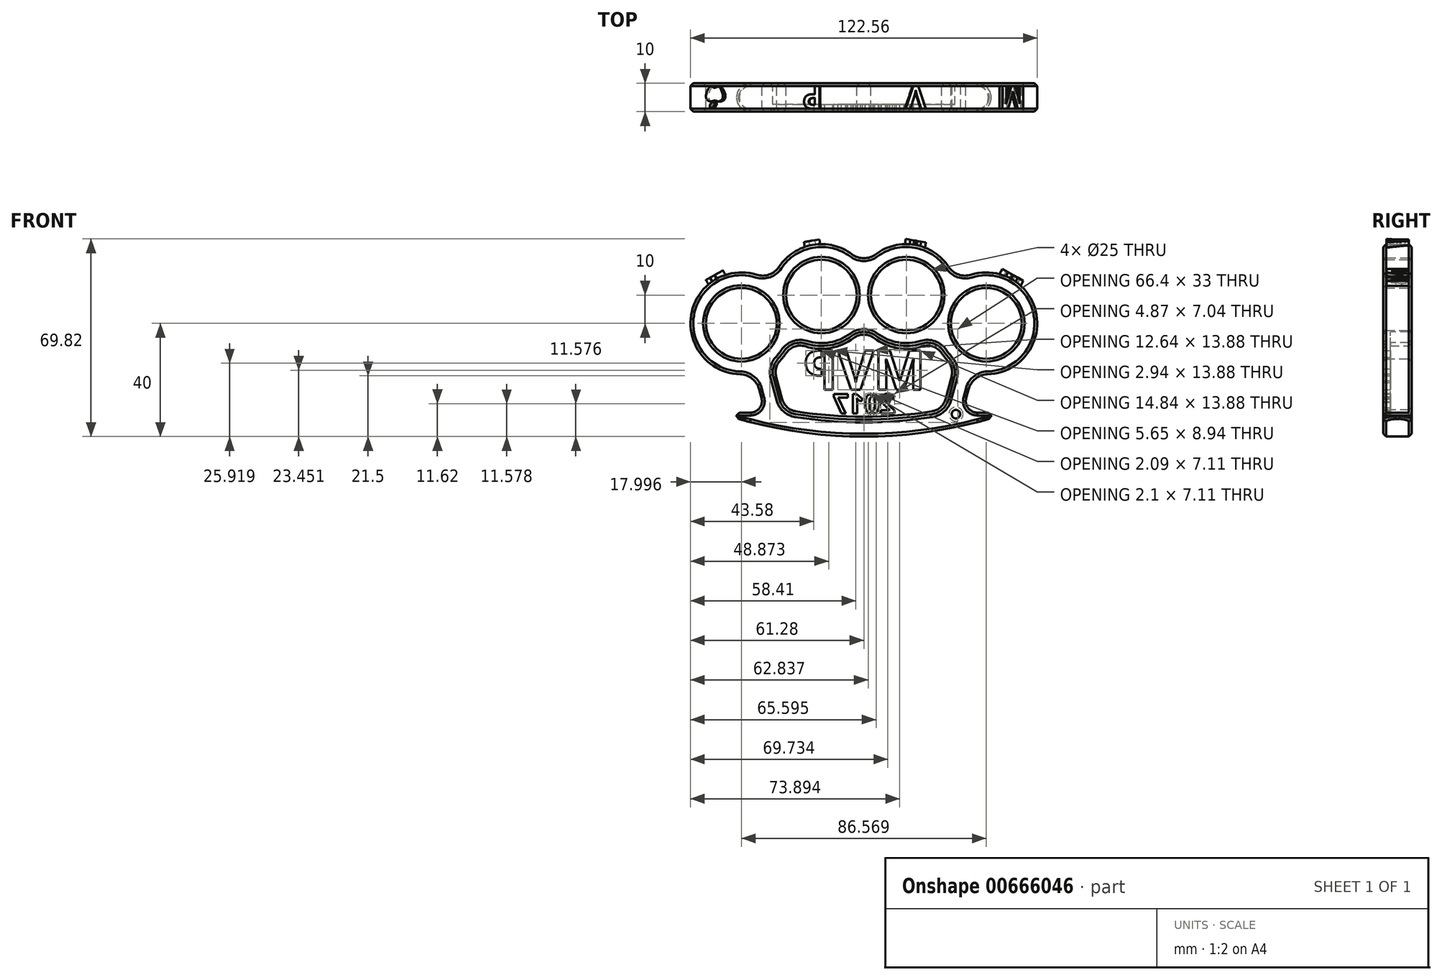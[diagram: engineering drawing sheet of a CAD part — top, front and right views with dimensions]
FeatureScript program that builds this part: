
annotation { "Feature Type Name" : "Feature", "Feature Type Description" : "" }
export const myFeature = defineFeature(function(context is Context, id is Id, definition is map)
    precondition{}
    {
        {
            var Q0;
            Q0=qCreatedBy(makeId("Front.planeOp"),FACE);
            var sketch = newSketch(context, id + "F0", { "sketchPlane" : qUnion([Q0])});
            skCircle(sketch, "E0", {"center": v(-43.28, 0) * mm, "radius": 12.5 * mm});
            skCircle(sketch, "E1", {"center": v(-15, 10) * mm, "radius": 12.5 * mm});
            skCircle(sketch, "E2", {"center": v(15, 10) * mm, "radius": 12.5 * mm});
            skCircle(sketch, "E3", {"center": v(43.28, 0) * mm, "radius": 12.5 * mm});
            skLineSegment(sketch, "E4", {"start": v(0, 38.87) * mm, "end": v(0, -56.1) * mm, "construction": true});
            skArc(sketch, "E5", {"start": v(-32.46, 14.38) * mm, "mid": v(-60.95, 3.43) * mm, "end": v(-38.63, -17.39) * mm});
            skArc(sketch, "E6", {"start": v(25.83, -4.38) * mm, "mid": v(28.5, -10.27) * mm, "end": v(33.1, -14.84) * mm});
            skArc(sketch, "E7.trimOffspring", {"start": v(-25.83, -4.38) * mm, "mid": v(-11.96, -7.74) * mm, "end": v(0, 0.05) * mm});
            skArc(sketch, "E8.trimOffspring", {"start": v(32.46, 14.38) * mm, "mid": v(18.04, 27.74) * mm, "end": v(0, 19.95) * mm});
            skArc(sketch, "E9.trimOffspring", {"start": v(0, 19.95) * mm, "mid": v(-18.04, 27.74) * mm, "end": v(-32.46, 14.38) * mm});
            skArc(sketch, "E10.trimOffspring", {"start": v(0, 0.05) * mm, "mid": v(11.96, -7.74) * mm, "end": v(25.83, -4.38) * mm});
            skArc(sketch, "E11", {"start": v(-45, -33.54) * mm, "mid": v(0, -40) * mm, "end": v(45, -33.54) * mm});
            skLineSegment(sketch, "E12", {"start": v(-45, -33.54) * mm, "end": v(-45, -31.54) * mm});
            skLineSegment(sketch, "E13", {"start": v(-36.18, -26.5) * mm, "end": v(-38.63, -17.39) * mm});
            skLineSegment(sketch, "E14", {"start": v(-45, -31.54) * mm, "end": v(-40.05, -31.54) * mm});
            skLineSegment(sketch, "E15.MirrorCS", {"start": v(45, -33.54) * mm, "end": v(45, -31.54) * mm});
            skPoint(sketch, "E16.visualSharp", {"position": v(-34.83, -31.54) * mm});
            skArc(sketch, "E16.filletArc", {"start": v(-40.05, -31.54) * mm, "mid": v(-36.87, -29.98) * mm, "end": v(-36.18, -26.5) * mm});
            skLineSegment(sketch, "E17.MirrorCS", {"start": v(36.18, -26.5) * mm, "end": v(38.63, -17.39) * mm});
            skLineSegment(sketch, "E18.MirrorCS", {"start": v(45, -31.54) * mm, "end": v(40.05, -31.54) * mm});
            skArc(sketch, "E19.MirrorCS", {"start": v(40.05, -31.54) * mm, "mid": v(36.87, -29.98) * mm, "end": v(36.18, -26.5) * mm});
            skArc(sketch, "E20", {"start": v(-28.68, -31.3) * mm, "mid": v(0, -34) * mm, "end": v(28.68, -31.3) * mm});
            skLineSegment(sketch, "E21", {"start": v(-28.68, -31.3) * mm, "end": v(-33.1, -14.84) * mm});
            skLineSegment(sketch, "E22", {"start": v(28.68, -31.3) * mm, "end": v(33.1, -14.84) * mm});
            skArc(sketch, "E23.trimOffspring", {"start": v(-33.1, -14.84) * mm, "mid": v(-28.5, -10.27) * mm, "end": v(-25.83, -4.38) * mm});
            skArc(sketch, "E24.trimOffspring", {"start": v(38.63, -17.39) * mm, "mid": v(60.95, 3.43) * mm, "end": v(32.46, 14.38) * mm});
            skSolve(sketch);
        }
        {
            var Q0;
            Q0=makeQuery(id+"F0.imprint","IMPRINT",FACE,{"disambiguationData":[TD([[makeQuery(id+"F0.imprint","IMPRINT",EDGE,{"derivedFrom":sQuery(id+"F0.wireOp",EDGE,"E0")}),-1.0]])]});
            extrude(context, id + "F1", {"entities" : qUnion([Q0]), "depth" : 10 * mm, "offsetDistance" : 25 * mm});
        }
        {
            var Q0;
            Q0=makeQuery(id+"F1.opExtrude","CAP_EDGE",EDGE,{"disambiguationData":[OSD([sQuery(id+"F0.wireOp",EDGE,"E12")])],"isStart":false});
            var Q1;
            Q1=makeQuery(id+"F1.opExtrude","CAP_EDGE",EDGE,{"disambiguationData":[OSD([sQuery(id+"F0.wireOp",EDGE,"E12")])],"isStart":true});
            var Q2;
            Q2=makeQuery(id+"F1.opExtrude","CAP_EDGE",EDGE,{"disambiguationData":[OSD([sQuery(id+"F0.wireOp",EDGE,"E15.MirrorCS")])],"isStart":false});
            var Q3;
            Q3=makeQuery(id+"F1.opExtrude","CAP_EDGE",EDGE,{"disambiguationData":[OSD([sQuery(id+"F0.wireOp",EDGE,"E15.MirrorCS")])],"isStart":true});
            fillet(context, id + "F2", {"entities" : qUnion([Q0, Q1, Q2, Q3]), "radius" : 5 * mm, "tangentPropagation" : true, "allowEdgeOverflow" : false});
        }
        {
            var Q0;
            Q0=makeQuery(id+"F1.opExtrude","SWEPT_EDGE",EDGE,{"disambiguationData":[OSD([sQuery(id+"F0.wireOp",EDGE,"E7.trimOffspring"),sQuery(id+"F0.wireOp",EDGE,"E23.trimOffspring")])]});
            var Q1;
            Q1=makeQuery(id+"F1.opExtrude","SWEPT_EDGE",EDGE,{"disambiguationData":[OSD([sQuery(id+"F0.wireOp",EDGE,"E7.trimOffspring"),sQuery(id+"F0.wireOp",EDGE,"E10.trimOffspring")])]});
            var Q2;
            Q2=makeQuery(id+"F1.opExtrude","SWEPT_EDGE",EDGE,{"disambiguationData":[OSD([sQuery(id+"F0.wireOp",EDGE,"E6"),sQuery(id+"F0.wireOp",EDGE,"E10.trimOffspring")])]});
            var Q3;
            Q3=makeQuery(id+"F1.opExtrude","SWEPT_EDGE",EDGE,{"disambiguationData":[OSD([sQuery(id+"F0.wireOp",EDGE,"E6"),sQuery(id+"F0.wireOp",EDGE,"E22")])]});
            var Q4;
            Q4=makeQuery(id+"F1.opExtrude","SWEPT_EDGE",EDGE,{"disambiguationData":[OSD([sQuery(id+"F0.wireOp",EDGE,"E21"),sQuery(id+"F0.wireOp",EDGE,"E23.trimOffspring")])]});
            var Q5;
            Q5=makeQuery(id+"F1.opExtrude","SWEPT_EDGE",EDGE,{"disambiguationData":[OSD([sQuery(id+"F0.wireOp",EDGE,"E8.trimOffspring"),sQuery(id+"F0.wireOp",EDGE,"E24.trimOffspring")])]});
            var Q6;
            Q6=makeQuery(id+"F1.opExtrude","SWEPT_EDGE",EDGE,{"disambiguationData":[OSD([sQuery(id+"F0.wireOp",EDGE,"E8.trimOffspring"),sQuery(id+"F0.wireOp",EDGE,"E9.trimOffspring")])]});
            var Q7;
            Q7=makeQuery(id+"F1.opExtrude","SWEPT_EDGE",EDGE,{"disambiguationData":[OSD([sQuery(id+"F0.wireOp",EDGE,"E5"),sQuery(id+"F0.wireOp",EDGE,"E9.trimOffspring")])]});
            var Q8;
            Q8=makeQuery(id+"F1.opExtrude","SWEPT_EDGE",EDGE,{"disambiguationData":[OSD([sQuery(id+"F0.wireOp",EDGE,"E20"),sQuery(id+"F0.wireOp",EDGE,"E21")])]});
            var Q9;
            Q9=makeQuery(id+"F1.opExtrude","SWEPT_EDGE",EDGE,{"disambiguationData":[OSD([sQuery(id+"F0.wireOp",EDGE,"E20"),sQuery(id+"F0.wireOp",EDGE,"E22")])]});
            var Q10;
            Q10=makeQuery(id+"F1.opExtrude","SWEPT_EDGE",EDGE,{"disambiguationData":[OSD([sQuery(id+"F0.wireOp",EDGE,"E5"),sQuery(id+"F0.wireOp",EDGE,"E13")])]});
            var Q11;
            Q11=makeQuery(id+"F1.opExtrude","SWEPT_EDGE",EDGE,{"disambiguationData":[OSD([sQuery(id+"F0.wireOp",EDGE,"E17.MirrorCS"),sQuery(id+"F0.wireOp",EDGE,"E24.trimOffspring")])]});
            fillet(context, id + "F3", {"entities" : qUnion([Q0, Q1, Q2, Q3, Q4, Q5, Q6, Q7, Q8, Q9, Q10, Q11]), "radius" : 7 * mm, "tangentPropagation" : true, "allowEdgeOverflow" : false});
        }
        {
            var Q0;
            Q0=qCreatedBy(makeId("Front.planeOp"),FACE);
            cPlane(context, id + "F4", {"entities" : qUnion([Q0]), "cplaneType" : CPlaneType.OFFSET, "offset" : 5 * mm, "width" : 150 * mm, "height" : 150 * mm});
        }
        {
            var Q0;
            Q0=makeQuery(id+"F1.opExtrude","CAP_FACE",FACE,{"disambiguationData":[OSD([sQuery(id+"F0.wireOp",EDGE,"E0"),sQuery(id+"F0.wireOp",EDGE,"E1"),sQuery(id+"F0.wireOp",EDGE,"E2"),sQuery(id+"F0.wireOp",EDGE,"E3"),sQuery(id+"F0.wireOp",EDGE,"E5"),sQuery(id+"F0.wireOp",EDGE,"E6"),sQuery(id+"F0.wireOp",EDGE,"E7.trimOffspring"),sQuery(id+"F0.wireOp",EDGE,"E8.trimOffspring"),sQuery(id+"F0.wireOp",EDGE,"E9.trimOffspring"),sQuery(id+"F0.wireOp",EDGE,"E10.trimOffspring"),sQuery(id+"F0.wireOp",EDGE,"E11"),sQuery(id+"F0.wireOp",EDGE,"E12"),sQuery(id+"F0.wireOp",EDGE,"E13"),sQuery(id+"F0.wireOp",EDGE,"E14"),sQuery(id+"F0.wireOp",EDGE,"E15.MirrorCS"),sQuery(id+"F0.wireOp",EDGE,"E16.filletArc"),sQuery(id+"F0.wireOp",EDGE,"E17.MirrorCS"),sQuery(id+"F0.wireOp",EDGE,"E18.MirrorCS"),sQuery(id+"F0.wireOp",EDGE,"E19.MirrorCS"),sQuery(id+"F0.wireOp",EDGE,"E20"),sQuery(id+"F0.wireOp",EDGE,"E21"),sQuery(id+"F0.wireOp",EDGE,"E22"),sQuery(id+"F0.wireOp",EDGE,"E23.trimOffspring"),sQuery(id+"F0.wireOp",EDGE,"E24.trimOffspring")])],"isStart":false});
            var sketch = newSketch(context, id + "F5", { "sketchPlane" : qUnion([Q0])});
            skLineSegment(sketch, "E25.0", {"start": v(-29.84, -26.99) * mm, "end": v(-31.96, -19.07) * mm});
            skArc(sketch, "E25.1", {"start": v(-24.18, -32.1) * mm, "mid": v(-27.76, -30.38) * mm, "end": v(-29.84, -26.99) * mm});
            skArc(sketch, "E25.2", {"start": v(-24.18, -32.1) * mm, "mid": v(0, -34) * mm, "end": v(24.18, -32.1) * mm});
            skArc(sketch, "E25.3", {"start": v(29.84, -26.99) * mm, "mid": v(27.76, -30.38) * mm, "end": v(24.18, -32.1) * mm});
            skLineSegment(sketch, "E25.4", {"start": v(29.84, -26.99) * mm, "end": v(31.96, -19.07) * mm});
            skArc(sketch, "E25.5", {"start": v(30.26, -12.43) * mm, "mid": v(31.98, -15.53) * mm, "end": v(31.96, -19.07) * mm});
            skArc(sketch, "E25.6", {"start": v(20.38, -7.18) * mm, "mid": v(24.8, -7.26) * mm, "end": v(28.3, -9.98) * mm});
            skArc(sketch, "E25.7", {"start": v(4.2, -4.4) * mm, "mid": v(11.96, -7.74) * mm, "end": v(20.38, -7.18) * mm});
            skArc(sketch, "E25.8", {"start": v(-4.2, -4.4) * mm, "mid": v(0, -3) * mm, "end": v(4.2, -4.4) * mm});
            skArc(sketch, "E25.9", {"start": v(-20.38, -7.18) * mm, "mid": v(-11.96, -7.74) * mm, "end": v(-4.2, -4.4) * mm});
            skArc(sketch, "E25.10", {"start": v(-28.3, -9.98) * mm, "mid": v(-24.8, -7.26) * mm, "end": v(-20.38, -7.18) * mm});
            skArc(sketch, "E25.11", {"start": v(-31.96, -19.07) * mm, "mid": v(-31.98, -15.53) * mm, "end": v(-30.26, -12.43) * mm});
            skArc(sketch, "E25.12", {"start": v(-30.26, -12.43) * mm, "mid": v(-29.23, -11.25) * mm, "end": v(-28.3, -9.98) * mm});
            skArc(sketch, "E25.13", {"start": v(28.3, -9.98) * mm, "mid": v(29.23, -11.25) * mm, "end": v(30.26, -12.43) * mm});
            skSolve(sketch);
        }
        {
            var Q0;
            Q0 = qSketchRegion(id + "F5", true);
            extrude(context, id + "F6", {"entities" : qUnion([Q0]), "operationType" : NewBodyOperationType.ADD, "oppositeDirection" : true, "depth" : 2.5 * mm, "offsetDistance" : 25 * mm});
        }
        {
            var Q0;
            Q0=makeQuery(id+"F6.opExtrude","CAP_FACE",FACE,{"disambiguationData":[OSD([sQuery(id+"F5.wireOp",EDGE,"E25.0"),sQuery(id+"F5.wireOp",EDGE,"E25.1"),sQuery(id+"F5.wireOp",EDGE,"E25.2"),sQuery(id+"F5.wireOp",EDGE,"E25.3"),sQuery(id+"F5.wireOp",EDGE,"E25.4"),sQuery(id+"F5.wireOp",EDGE,"E25.5"),sQuery(id+"F5.wireOp",EDGE,"E25.6"),sQuery(id+"F5.wireOp",EDGE,"E25.7"),sQuery(id+"F5.wireOp",EDGE,"E25.8"),sQuery(id+"F5.wireOp",EDGE,"E25.9"),sQuery(id+"F5.wireOp",EDGE,"E25.10"),sQuery(id+"F5.wireOp",EDGE,"E25.11"),sQuery(id+"F5.wireOp",EDGE,"E25.12"),sQuery(id+"F5.wireOp",EDGE,"E25.13")])],"isStart":false});
            var sketch = newSketch(context, id + "F7", { "sketchPlane" : qUnion([Q0])});
            skText(sketch, "E26", { "text": "MVP", "fontName": "OpenSans-Bold.ttf"});
            skText(sketch, "E27", { "text": "2017", "fontName": "OpenSans-Bold.ttf"});
            const initialGuessF7  = {"E26": [-0.02178, -0.02349, 1, 0, 0.014], "E27": [-0.01126, -0.0319, 1, 0, 0.007]};
            skSetInitialGuess(sketch, initialGuessF7);
            skSolve(sketch);
        }
        {
            var Q0;
            Q0 = qSketchRegion(id + "F7", true);
            extrude(context, id + "F8", {"entities" : qUnion([Q0]), "operationType" : NewBodyOperationType.REMOVE, "oppositeDirection" : true, "depth" : 25 * mm, "offsetDistance" : 25 * mm});
        }
        {
            var Q0;
            Q0=makeQuery(id+"F1.opExtrude","CAP_EDGE",EDGE,{"disambiguationData":[OSD([sQuery(id+"F0.wireOp",EDGE,"E5")])],"isStart":false});
            var Q1;
            Q1=makeQuery(id+"F1.opExtrude","CAP_EDGE",EDGE,{"disambiguationData":[OSD([sQuery(id+"F0.wireOp",EDGE,"E11")])],"isStart":false});
            var Q2;
            Q2=makeQuery(id+"F1.opExtrude","CAP_EDGE",EDGE,{"disambiguationData":[OSD([sQuery(id+"F0.wireOp",EDGE,"E21")])],"isStart":false});
            var Q3;
            Q3=makeQuery(id+"F1.opExtrude","CAP_EDGE",EDGE,{"disambiguationData":[OSD([sQuery(id+"F0.wireOp",EDGE,"E0")])],"isStart":false});
            var Q4;
            Q4=makeQuery(id+"F1.opExtrude","CAP_EDGE",EDGE,{"disambiguationData":[OSD([sQuery(id+"F0.wireOp",EDGE,"E1")])],"isStart":false});
            var Q5;
            Q5=makeQuery(id+"F1.opExtrude","CAP_EDGE",EDGE,{"disambiguationData":[OSD([sQuery(id+"F0.wireOp",EDGE,"E2")])],"isStart":false});
            var Q6;
            Q6=makeQuery(id+"F1.opExtrude","CAP_EDGE",EDGE,{"disambiguationData":[OSD([sQuery(id+"F0.wireOp",EDGE,"E3")])],"isStart":false});
            var Q7;
            Q7=makeQuery(id+"F1.opExtrude","CAP_EDGE",EDGE,{"disambiguationData":[OSD([sQuery(id+"F0.wireOp",EDGE,"E3")])],"isStart":true});
            var Q8;
            Q8=makeQuery(id+"F1.opExtrude","CAP_EDGE",EDGE,{"disambiguationData":[OSD([sQuery(id+"F0.wireOp",EDGE,"E2")])],"isStart":true});
            var Q9;
            Q9=makeQuery(id+"F1.opExtrude","CAP_EDGE",EDGE,{"disambiguationData":[OSD([sQuery(id+"F0.wireOp",EDGE,"E1")])],"isStart":true});
            var Q10;
            Q10=makeQuery(id+"F1.opExtrude","CAP_EDGE",EDGE,{"disambiguationData":[OSD([sQuery(id+"F0.wireOp",EDGE,"E0")])],"isStart":true});
            var Q11;
            Q11=makeQuery(id+"F1.opExtrude","CAP_EDGE",EDGE,{"disambiguationData":[OSD([sQuery(id+"F0.wireOp",EDGE,"E22")])],"isStart":true});
            var Q12;
            Q12=makeQuery(id+"F6.opExtrude","CAP_EDGE",EDGE,{"disambiguationData":[OSD([sQuery(id+"F5.wireOp",EDGE,"E25.4")])],"isStart":true});
            var Q13;
            Q13=makeQuery(id+"F6.opExtrude","CAP_EDGE",EDGE,{"disambiguationData":[OSD([sQuery(id+"F5.wireOp",EDGE,"E25.5")])],"isStart":false});
            chamfer(context, id + "F9", {"entities" : qUnion([Q0, Q1, Q2, Q3, Q4, Q5, Q6, Q7, Q8, Q9, Q10, Q11, Q12, Q13]), "width" : 1 * mm, "tangentPropagation" : true});
        }
        {
            var Q0;
            Q0=qCreatedBy(id+"F4.planeOp",FACE);
            var sketch = newSketch(context, id + "F10", { "sketchPlane" : qUnion([Q0])});
            skLineSegment(sketch, "E28", {"start": v(0, -77.43) * mm, "end": v(19.89, 38.49) * mm, "construction": true});
            skLineSegment(sketch, "E29", {"start": v(0, 38.45) * mm, "end": v(0, -77.43) * mm, "construction": true});
            skLineSegment(sketch, "E30", {"start": v(0, -77.43) * mm, "end": v(-64.72, 38.35) * mm, "construction": true});
            skLineSegment(sketch, "E31", {"start": v(0, -77.43) * mm, "end": v(63.92, 36.9) * mm, "construction": true});
            skCircle(sketch, "E32.0", {"center": v(-43.28, 0) * mm, "radius": 12.5 * mm});
            skCircle(sketch, "E33.0", {"center": v(43.28, 0) * mm, "radius": 12.5 * mm});
            skPoint(sketch, "E34", {"position": v(-52.07, 15.71) * mm});
            skPoint(sketch, "E35", {"position": v(-18.04, 27.74) * mm});
            skPoint(sketch, "E36", {"position": v(18.04, 27.74) * mm});
            skPoint(sketch, "E37", {"position": v(52.07, 15.71) * mm});
            skLineSegment(sketch, "E38", {"start": v(0, -77.43) * mm, "end": v(-21.26, 46.47) * mm, "construction": true});
            skCircle(sketch, "E39.0", {"center": v(-15, 10) * mm, "radius": 12.5 * mm});
            skSolve(sketch);
        }
        {
            var Q0;
            Q0=sQuery(id+"F10.wireOp",VERTEX,"E34");
            var Q1;
            Q1=sQuery(id+"F10.wireOp",EDGE,"E30");
            cPlane(context, id + "F11", {"entities" : qUnion([Q0, Q1]), "cplaneType" : CPlaneType.LINE_POINT, "offset" : 25 * mm, "width" : 150 * mm, "height" : 150 * mm});
        }
        {
            var Q0;
            Q0=sQuery(id+"F10.wireOp",EDGE,"E38");
            var Q1;
            Q1=sQuery(id+"F10.wireOp",VERTEX,"E35");
            cPlane(context, id + "F12", {"entities" : qUnion([Q0, Q1]), "cplaneType" : CPlaneType.LINE_POINT, "offset" : 25 * mm, "width" : 150 * mm, "height" : 150 * mm});
        }
        {
            var Q0;
            Q0=sQuery(id+"F10.wireOp",VERTEX,"E36");
            var Q1;
            Q1=sQuery(id+"F10.wireOp",EDGE,"E28");
            cPlane(context, id + "F13", {"entities" : qUnion([Q0, Q1]), "cplaneType" : CPlaneType.LINE_POINT, "offset" : 25 * mm, "width" : 150 * mm, "height" : 150 * mm});
        }
        {
            var Q0;
            Q0=sQuery(id+"F10.wireOp",VERTEX,"E37");
            var Q1;
            Q1=sQuery(id+"F10.wireOp",EDGE,"E31");
            cPlane(context, id + "F14", {"entities" : qUnion([Q0, Q1]), "cplaneType" : CPlaneType.LINE_POINT, "offset" : 25 * mm, "width" : 150 * mm, "height" : 150 * mm});
        }
        {
            var Q0;
            Q0=qCreatedBy(id+"F14.planeOp",FACE);
            var sketch = newSketch(context, id + "F15", { "sketchPlane" : qUnion([Q0])});
            skText(sketch, "E40", { "text": "M", "fontName": "OpenSans-Bold.ttf"});
            skLineSegment(sketch, "E41", {"start": v(42.88, -1) * mm, "end": v(73.13, -1) * mm});
            const initialGuessF15  = {"E40": [0.04288, -0.001, -1, 0, 0.008]};
            skSetInitialGuess(sketch, initialGuessF15);
            skSolve(sketch);
        }
        {
            var Q0;
            Q0=qCreatedBy(id+"F13.planeOp",FACE);
            var sketch = newSketch(context, id + "F16", { "sketchPlane" : qUnion([Q0])});
            skText(sketch, "E42", { "text": "V", "fontName": "OpenSans-Bold.ttf"});
            skLineSegment(sketch, "E43", {"start": v(13.53, -1) * mm, "end": v(16.76, -1) * mm});
            const initialGuessF16  = {"E42": [0.01676, -0.001, -1, 0, 0.008]};
            skSetInitialGuess(sketch, initialGuessF16);
            skSolve(sketch);
        }
        {
            var Q0;
            Q0=qCreatedBy(id+"F12.planeOp",FACE);
            var sketch = newSketch(context, id + "F17", { "sketchPlane" : qUnion([Q0])});
            skText(sketch, "E44", { "text": "P", "fontName": "OpenSans-Bold.ttf"});
            skLineSegment(sketch, "E45", {"start": v(-9.5, -1) * mm, "end": v(27.08, -1) * mm});
            const initialGuessF17  = {"E44": [-0.0095, -0.001, -1, 0, 0.008]};
            skSetInitialGuess(sketch, initialGuessF17);
            skSolve(sketch);
        }
        {
            var Q0;
            Q0=qCreatedBy(id+"F11.planeOp",FACE);
            var sketch = newSketch(context, id + "F18", { "sketchPlane" : qUnion([Q0])});
            skLineSegment(sketch, "E46", {"start": v(-37.78, 4.33) * mm, "end": v(-37.78, -21.33) * mm, "construction": true});
            skFitSpline(sketch, "E47", {"points": [v(-37.78, -1.74) * mm, v(-39.38, -1.13) * mm, v(-40.33, -2.03) * mm, v(-41.18, -4.15) * mm, v(-40.94, -5.57) * mm, v(-39.59, -6.37) * mm, v(-37.78, -6) * mm], "startDerivative": vector(-11.84, 8.82) * mm, "endDerivative": vector(10.4, 4.73) * mm});
            skPoint(sketch, "E48", {"position": v(-37.78, -8.5) * mm});
            skFitSpline(sketch, "E49.MirrorCS", {"points": [v(-37.78, -1.74) * mm, v(-36.18, -1.13) * mm, v(-35.23, -2.03) * mm, v(-34.38, -4.15) * mm, v(-34.63, -5.57) * mm, v(-35.97, -6.37) * mm, v(-37.78, -6) * mm], "startDerivative": vector(11.84, 8.82) * mm, "endDerivative": vector(-10.4, 4.73) * mm});
            skArc(sketch, "E50.filletArc", {"start": v(-38.29, -1.4) * mm, "mid": v(-37.78, -1.54) * mm, "end": v(-37.27, -1.4) * mm});
            skArc(sketch, "E51.filletArc", {"start": v(-37.43, -6.16) * mm, "mid": v(-37.78, -6.1) * mm, "end": v(-38.13, -6.16) * mm});
            skArc(sketch, "E52", {"start": v(-37.78, -6.5) * mm, "mid": v(-39.26, -7.12) * mm, "end": v(-39.57, -8.7) * mm});
            skArc(sketch, "E53", {"start": v(-39.57, -8.7) * mm, "mid": v(-38.07, -8.1) * mm, "end": v(-37.78, -6.5) * mm});
            skSolve(sketch);
        }
        {
            var Q0;
            Q0 = qSketchRegion(id + "F18", true);
            extrude(context, id + "F19", {"entities" : qUnion([Q0]), "operationType" : NewBodyOperationType.ADD, "depth" : 1.5 * mm, "offsetDistance" : 25 * mm, "hasSecondDirection" : true, "secondDirectionBound" : SecondDirectionBoundingType.UP_TO_NEXT, "secondDirectionOppositeDirection" : true, "secondDirectionDepth" : 25 * mm});
        }
        {
            var Q0;
            Q0 = qSketchRegion(id + "F17", true);
            extrude(context, id + "F20", {"entities" : qUnion([Q0]), "operationType" : NewBodyOperationType.ADD, "depth" : 1.5 * mm, "offsetDistance" : 25 * mm, "hasSecondDirection" : true, "secondDirectionBound" : SecondDirectionBoundingType.UP_TO_NEXT, "secondDirectionOppositeDirection" : true, "secondDirectionDepth" : 25 * mm});
        }
        {
            var Q0;
            Q0 = qSketchRegion(id + "F16", true);
            extrude(context, id + "F21", {"entities" : qUnion([Q0]), "operationType" : NewBodyOperationType.ADD, "depth" : 1.5 * mm, "offsetDistance" : 25 * mm, "hasSecondDirection" : true, "secondDirectionBound" : SecondDirectionBoundingType.UP_TO_NEXT, "secondDirectionOppositeDirection" : true, "secondDirectionDepth" : 25 * mm});
        }
        {
            var Q0;
            Q0 = qSketchRegion(id + "F15", true);
            extrude(context, id + "F22", {"entities" : qUnion([Q0]), "operationType" : NewBodyOperationType.ADD, "depth" : 1.5 * mm, "offsetDistance" : 25 * mm, "hasSecondDirection" : true, "secondDirectionBound" : SecondDirectionBoundingType.UP_TO_NEXT, "secondDirectionOppositeDirection" : true, "secondDirectionDepth" : 25 * mm});
        }
        {
            var Q0;
            Q0=makeQuery(id+"F1.opExtrude","CAP_FACE",FACE,{"disambiguationData":[OSD([sQuery(id+"F0.wireOp",EDGE,"E0"),sQuery(id+"F0.wireOp",EDGE,"E1"),sQuery(id+"F0.wireOp",EDGE,"E2"),sQuery(id+"F0.wireOp",EDGE,"E3"),sQuery(id+"F0.wireOp",EDGE,"E5"),sQuery(id+"F0.wireOp",EDGE,"E6"),sQuery(id+"F0.wireOp",EDGE,"E7.trimOffspring"),sQuery(id+"F0.wireOp",EDGE,"E8.trimOffspring"),sQuery(id+"F0.wireOp",EDGE,"E9.trimOffspring"),sQuery(id+"F0.wireOp",EDGE,"E10.trimOffspring"),sQuery(id+"F0.wireOp",EDGE,"E11"),sQuery(id+"F0.wireOp",EDGE,"E12"),sQuery(id+"F0.wireOp",EDGE,"E13"),sQuery(id+"F0.wireOp",EDGE,"E14"),sQuery(id+"F0.wireOp",EDGE,"E15.MirrorCS"),sQuery(id+"F0.wireOp",EDGE,"E16.filletArc"),sQuery(id+"F0.wireOp",EDGE,"E17.MirrorCS"),sQuery(id+"F0.wireOp",EDGE,"E18.MirrorCS"),sQuery(id+"F0.wireOp",EDGE,"E19.MirrorCS"),sQuery(id+"F0.wireOp",EDGE,"E20"),sQuery(id+"F0.wireOp",EDGE,"E21"),sQuery(id+"F0.wireOp",EDGE,"E22"),sQuery(id+"F0.wireOp",EDGE,"E23.trimOffspring"),sQuery(id+"F0.wireOp",EDGE,"E24.trimOffspring")])],"isStart":false});
            var sketch = newSketch(context, id + "F23", { "sketchPlane" : qUnion([Q0])});
            skCircle(sketch, "E54", {"center": v(32.55, -32.09) * mm, "radius": 1.5 * mm});
            skSolve(sketch);
        }
        {
            var Q0;
            Q0=makeQuery(id+"F23.imprint","IMPRINT",FACE,{"disambiguationData":[TD([[makeQuery(id+"F23.imprint","IMPRINT",EDGE,{"derivedFrom":sQuery(id+"F23.wireOp",EDGE,"E54")}),1.0]])]});
            extrude(context, id + "F24", {"entities" : qUnion([Q0]), "operationType" : NewBodyOperationType.REMOVE, "oppositeDirection" : true, "depth" : 25 * mm, "offsetDistance" : 25 * mm});
        }
        {
            var Q0;
            Q0=makeQuery(id+"F24.boolean.opBoolean","COPY",EDGE,{"derivedFrom":makeQuery(id+"F24.opExtrude","CAP_EDGE",EDGE,{"disambiguationData":[OSD([sQuery(id+"F23.wireOp",EDGE,"E54")])],"isStart":true})});
            var Q1;
            Q1=makeQuery(id+"F24.boolean.opBoolean","INTERSECT",EDGE,{"derivedFrom":[makeQuery(id+"F1.opExtrude","CAP_FACE",FACE,{"disambiguationData":[OSD([sQuery(id+"F0.wireOp",EDGE,"E0"),sQuery(id+"F0.wireOp",EDGE,"E1"),sQuery(id+"F0.wireOp",EDGE,"E2"),sQuery(id+"F0.wireOp",EDGE,"E3"),sQuery(id+"F0.wireOp",EDGE,"E5"),sQuery(id+"F0.wireOp",EDGE,"E6"),sQuery(id+"F0.wireOp",EDGE,"E7.trimOffspring"),sQuery(id+"F0.wireOp",EDGE,"E8.trimOffspring"),sQuery(id+"F0.wireOp",EDGE,"E9.trimOffspring"),sQuery(id+"F0.wireOp",EDGE,"E10.trimOffspring"),sQuery(id+"F0.wireOp",EDGE,"E11"),sQuery(id+"F0.wireOp",EDGE,"E12"),sQuery(id+"F0.wireOp",EDGE,"E13"),sQuery(id+"F0.wireOp",EDGE,"E14"),sQuery(id+"F0.wireOp",EDGE,"E15.MirrorCS"),sQuery(id+"F0.wireOp",EDGE,"E16.filletArc"),sQuery(id+"F0.wireOp",EDGE,"E17.MirrorCS"),sQuery(id+"F0.wireOp",EDGE,"E18.MirrorCS"),sQuery(id+"F0.wireOp",EDGE,"E19.MirrorCS"),sQuery(id+"F0.wireOp",EDGE,"E20"),sQuery(id+"F0.wireOp",EDGE,"E21"),sQuery(id+"F0.wireOp",EDGE,"E22"),sQuery(id+"F0.wireOp",EDGE,"E23.trimOffspring"),sQuery(id+"F0.wireOp",EDGE,"E24.trimOffspring")])],"isStart":true}),makeQuery(id+"F24.opExtrude","SWEPT_FACE",FACE,{"disambiguationData":[OSD([sQuery(id+"F23.wireOp",EDGE,"E54")])]})]});
            chamfer(context, id + "F25", {"entities" : qUnion([Q0, Q1]), "width" : 1 * mm, "tangentPropagation" : true});
        }
        {
            var Q0;
            {var subQ6=sQuery(id+"F0.wireOp",EDGE,"E6");Q0=makeQuery(id+"F8.boolean.opBoolean","SPLIT",FACE,{"disambiguationData":[TD([makeQuery(id+"F1.opExtrude","SWEPT_FACE",FACE,{"disambiguationData":[OSD([subQ6])]})])],"derivedFrom":makeQuery(id+"F6.opExtrude","CAP_FACE",FACE,{"disambiguationData":[OSD([sQuery(id+"F5.wireOp",EDGE,"E25.0"),sQuery(id+"F5.wireOp",EDGE,"E25.1"),sQuery(id+"F5.wireOp",EDGE,"E25.2"),sQuery(id+"F5.wireOp",EDGE,"E25.3"),sQuery(id+"F5.wireOp",EDGE,"E25.4"),sQuery(id+"F5.wireOp",EDGE,"E25.5"),sQuery(id+"F5.wireOp",EDGE,"E25.6"),sQuery(id+"F5.wireOp",EDGE,"E25.7"),sQuery(id+"F5.wireOp",EDGE,"E25.8"),sQuery(id+"F5.wireOp",EDGE,"E25.9"),sQuery(id+"F5.wireOp",EDGE,"E25.10"),sQuery(id+"F5.wireOp",EDGE,"E25.11"),sQuery(id+"F5.wireOp",EDGE,"E25.12"),sQuery(id+"F5.wireOp",EDGE,"E25.13")])],"isStart":false})});}
            var sketch = newSketch(context, id + "F26", { "sketchPlane" : qUnion([Q0])});
            skLineSegment(sketch, "E55", {"start": v(13.88, -18.55) * mm, "end": v(13.88, -9.6) * mm});
            skLineSegment(sketch, "E56", {"start": v(13.88, -9.6) * mm, "end": v(14.88, -9.6) * mm});
            skLineSegment(sketch, "E57", {"start": v(14.88, -9.6) * mm, "end": v(14.88, -18.55) * mm});
            skLineSegment(sketch, "E58", {"start": v(15.14, -18.55) * mm, "end": v(13.88, -18.55) * mm});
            skLineSegment(sketch, "E59.bottom", {"start": v(-3.27, -24.64) * mm, "end": v(-2.6, -24.64) * mm});
            skLineSegment(sketch, "E59.top", {"start": v(-3.27, -32.5) * mm, "end": v(-2.6, -32.5) * mm});
            skLineSegment(sketch, "E59.left", {"start": v(-3.27, -24.64) * mm, "end": v(-3.27, -32.5) * mm});
            skLineSegment(sketch, "E59.right", {"start": v(-2.6, -24.64) * mm, "end": v(-2.6, -32.5) * mm});
            skLineSegment(sketch, "E60", {"start": v(-2.94, -23.5) * mm, "end": v(-2.94, -36.08) * mm, "construction": true});
            skSolve(sketch);
        }
        {
            var Q0;
            Q0 = qSketchRegion(id + "F26", true);
            var Q1;
            {var subQ0=sQuery(id+"F0.wireOp",EDGE,"E17.MirrorCS");var subQ1=sQuery(id+"F0.wireOp",EDGE,"E9.trimOffspring");var subQ2=sQuery(id+"F0.wireOp",EDGE,"E5");var subQ3=sQuery(id+"F0.wireOp",EDGE,"E24.trimOffspring");var subQ4=sQuery(id+"F0.wireOp",EDGE,"E8.trimOffspring");var subQ5=sQuery(id+"F0.wireOp",EDGE,"E12");var subQ6=sQuery(id+"F0.wireOp",EDGE,"E13");var subQ7=sQuery(id+"F0.wireOp",EDGE,"E2");var subQ8=sQuery(id+"F0.wireOp",EDGE,"E15.MirrorCS");var subQ9=sQuery(id+"F0.wireOp",EDGE,"E1");var subQ10=sQuery(id+"F0.wireOp",EDGE,"E19.MirrorCS");var subQ11=sQuery(id+"F0.wireOp",EDGE,"E3");var subQ12=sQuery(id+"F0.wireOp",EDGE,"E0");var subQ13=sQuery(id+"F0.wireOp",EDGE,"E16.filletArc");var subQ14=sQuery(id+"F0.wireOp",EDGE,"E11");Q1=makeQuery(id+"F8.boolean.opBoolean","SPLIT",FACE,{"disambiguationData":[TD([makeQuery(id+"F1.opExtrude","SWEPT_FACE",FACE,{"disambiguationData":[OSD([subQ12])]})])],"derivedFrom":makeQuery(id+"F6.boolean.opBoolean","MERGE",FACE,{"derivedFrom":[makeQuery(id+"F1.opExtrude","CAP_FACE",FACE,{"disambiguationData":[OSD([subQ12,subQ9,subQ7,subQ11,subQ2,sQuery(id+"F0.wireOp",EDGE,"E6"),sQuery(id+"F0.wireOp",EDGE,"E7.trimOffspring"),subQ4,subQ1,sQuery(id+"F0.wireOp",EDGE,"E10.trimOffspring"),subQ14,subQ5,subQ6,sQuery(id+"F0.wireOp",EDGE,"E14"),subQ8,subQ13,subQ0,sQuery(id+"F0.wireOp",EDGE,"E18.MirrorCS"),subQ10,sQuery(id+"F0.wireOp",EDGE,"E20"),sQuery(id+"F0.wireOp",EDGE,"E21"),sQuery(id+"F0.wireOp",EDGE,"E22"),sQuery(id+"F0.wireOp",EDGE,"E23.trimOffspring"),subQ3])],"isStart":true}),makeQuery(id+"F6.opExtrude","CAP_FACE",FACE,{"disambiguationData":[OSD([sQuery(id+"F5.wireOp",EDGE,"E25.0"),sQuery(id+"F5.wireOp",EDGE,"E25.1"),sQuery(id+"F5.wireOp",EDGE,"E25.2"),sQuery(id+"F5.wireOp",EDGE,"E25.3"),sQuery(id+"F5.wireOp",EDGE,"E25.4"),sQuery(id+"F5.wireOp",EDGE,"E25.5"),sQuery(id+"F5.wireOp",EDGE,"E25.6"),sQuery(id+"F5.wireOp",EDGE,"E25.7"),sQuery(id+"F5.wireOp",EDGE,"E25.8"),sQuery(id+"F5.wireOp",EDGE,"E25.9"),sQuery(id+"F5.wireOp",EDGE,"E25.10"),sQuery(id+"F5.wireOp",EDGE,"E25.11"),sQuery(id+"F5.wireOp",EDGE,"E25.12"),sQuery(id+"F5.wireOp",EDGE,"E25.13")])],"isStart":true})]})});}
            extrude(context, id + "F27", {"entities" : qUnion([Q0]), "operationType" : NewBodyOperationType.ADD, "endBound" : BoundingType.UP_TO_SURFACE, "oppositeDirection" : true, "depth" : 25 * mm, "endBoundEntityFace" : qUnion([Q1]), "offsetDistance" : 25 * mm});
        }
        {
            var Q0;
            {var subQ0=sQuery(id+"F5.wireOp",EDGE,"E25.13");var subQ1=sQuery(id+"F5.wireOp",EDGE,"E25.12");var subQ2=sQuery(id+"F5.wireOp",EDGE,"E25.11");var subQ3=sQuery(id+"F5.wireOp",EDGE,"E25.10");var subQ4=sQuery(id+"F5.wireOp",EDGE,"E25.9");var subQ5=sQuery(id+"F5.wireOp",EDGE,"E25.8");var subQ6=sQuery(id+"F5.wireOp",EDGE,"E25.7");var subQ7=sQuery(id+"F5.wireOp",EDGE,"E25.6");var subQ8=sQuery(id+"F5.wireOp",EDGE,"E25.5");var subQ9=sQuery(id+"F5.wireOp",EDGE,"E25.4");var subQ10=sQuery(id+"F5.wireOp",EDGE,"E25.3");var subQ11=sQuery(id+"F5.wireOp",EDGE,"E25.2");var subQ12=sQuery(id+"F5.wireOp",EDGE,"E25.1");var subQ13=sQuery(id+"F5.wireOp",EDGE,"E25.0");var subQ14=sQuery(id+"F0.wireOp",EDGE,"E24.trimOffspring");var subQ15=sQuery(id+"F0.wireOp",EDGE,"E23.trimOffspring");var subQ16=sQuery(id+"F0.wireOp",EDGE,"E22");var subQ17=sQuery(id+"F0.wireOp",EDGE,"E21");var subQ18=sQuery(id+"F0.wireOp",EDGE,"E20");var subQ19=sQuery(id+"F0.wireOp",EDGE,"E19.MirrorCS");var subQ20=sQuery(id+"F0.wireOp",EDGE,"E18.MirrorCS");var subQ21=sQuery(id+"F0.wireOp",EDGE,"E17.MirrorCS");var subQ22=sQuery(id+"F0.wireOp",EDGE,"E16.filletArc");var subQ23=sQuery(id+"F0.wireOp",EDGE,"E15.MirrorCS");var subQ24=sQuery(id+"F0.wireOp",EDGE,"E14");var subQ25=sQuery(id+"F0.wireOp",EDGE,"E13");var subQ26=sQuery(id+"F0.wireOp",EDGE,"E12");var subQ27=sQuery(id+"F0.wireOp",EDGE,"E11");var subQ28=sQuery(id+"F0.wireOp",EDGE,"E10.trimOffspring");var subQ29=sQuery(id+"F0.wireOp",EDGE,"E9.trimOffspring");var subQ30=sQuery(id+"F0.wireOp",EDGE,"E8.trimOffspring");var subQ31=sQuery(id+"F0.wireOp",EDGE,"E7.trimOffspring");var subQ32=sQuery(id+"F0.wireOp",EDGE,"E6");var subQ33=sQuery(id+"F0.wireOp",EDGE,"E5");var subQ34=sQuery(id+"F0.wireOp",EDGE,"E3");var subQ35=sQuery(id+"F0.wireOp",EDGE,"E2");var subQ36=sQuery(id+"F0.wireOp",EDGE,"E1");var subQ37=sQuery(id+"F0.wireOp",EDGE,"E0");var subQ38=makeQuery(id+"F6.boolean.opBoolean","MERGE",FACE,{"derivedFrom":[makeQuery(id+"F1.opExtrude","CAP_FACE",FACE,{"disambiguationData":[OSD([subQ37,subQ36,subQ35,subQ34,subQ33,subQ32,subQ31,subQ30,subQ29,subQ28,subQ27,subQ26,subQ25,subQ24,subQ23,subQ22,subQ21,subQ20,subQ19,subQ18,subQ17,subQ16,subQ15,subQ14])],"isStart":true}),makeQuery(id+"F6.opExtrude","CAP_FACE",FACE,{"disambiguationData":[OSD([subQ13,subQ12,subQ11,subQ10,subQ9,subQ8,subQ7,subQ6,subQ5,subQ4,subQ3,subQ2,subQ1,subQ0])],"isStart":true})]});Q0=makeQuery(id+"F27.boolean.opBoolean","MERGE",FACE,{"derivedFrom":[makeQuery(id+"F8.boolean.opBoolean","SPLIT",FACE,{"disambiguationData":[TD([makeQuery(id+"F8.opExtrude","SWEPT_FACE",FACE,{"disambiguationData":[OSD([sQuery(id+"F7.wireOp",EDGE,"E26.sketch_text.stroke-29")])]})])],"derivedFrom":subQ38}),makeQuery(id+"F8.boolean.opBoolean","SPLIT",FACE,{"disambiguationData":[TD([makeQuery(id+"F8.opExtrude","SWEPT_FACE",FACE,{"disambiguationData":[OSD([sQuery(id+"F7.wireOp",EDGE,"E27.sketch_text.stroke-32")])]})])],"derivedFrom":subQ38}),makeQuery(id+"F8.boolean.opBoolean","SPLIT",FACE,{"disambiguationData":[TD([makeQuery(id+"F1.opExtrude","SWEPT_FACE",FACE,{"disambiguationData":[OSD([subQ37])]})])],"derivedFrom":subQ38}),makeQuery(id+"F27.opExtrude","CAP_FACE",FACE,{"disambiguationData":[OSD([subQ37,subQ36,subQ35,subQ34,subQ33,subQ32,subQ31,subQ30,subQ29,subQ28,subQ27,subQ26,subQ25,subQ24,subQ23,subQ22,subQ21,subQ20,subQ19,subQ18,subQ17,subQ16,subQ15,subQ14,subQ13,subQ12,subQ11,subQ10,subQ9,subQ8,subQ7,subQ6,subQ5,subQ4,subQ3,subQ2,subQ1,subQ0]),OD(0.0)],"isStart":false}),makeQuery(id+"F27.opExtrude","CAP_FACE",FACE,{"disambiguationData":[OSD([subQ37,subQ36,subQ35,subQ34,subQ33,subQ32,subQ31,subQ30,subQ29,subQ28,subQ27,subQ26,subQ25,subQ24,subQ23,subQ22,subQ21,subQ20,subQ19,subQ18,subQ17,subQ16,subQ15,subQ14,subQ13,subQ12,subQ11,subQ10,subQ9,subQ8,subQ7,subQ6,subQ5,subQ4,subQ3,subQ2,subQ1,subQ0]),OD(1.0)],"isStart":false})]});}
            var sketch = newSketch(context, id + "F28", { "sketchPlane" : qUnion([Q0])});
            skLineSegment(sketch, "E61.0", {"start": v(-31.96, -19.07) * mm, "end": v(-29.84, -26.99) * mm});
            skArc(sketch, "E62.0", {"start": v(-30.26, -12.43) * mm, "mid": v(-31.98, -15.53) * mm, "end": v(-31.96, -19.07) * mm});
            skArc(sketch, "E63.0", {"start": v(-28.3, -9.98) * mm, "mid": v(-29.23, -11.25) * mm, "end": v(-30.26, -12.43) * mm});
            skArc(sketch, "E64.0", {"start": v(-20.38, -7.18) * mm, "mid": v(-24.8, -7.26) * mm, "end": v(-28.3, -9.98) * mm});
            skArc(sketch, "E65.0", {"start": v(-4.2, -4.4) * mm, "mid": v(-11.96, -7.74) * mm, "end": v(-20.38, -7.18) * mm});
            skArc(sketch, "E66.0", {"start": v(4.2, -4.4) * mm, "mid": v(0, -3) * mm, "end": v(-4.2, -4.4) * mm});
            skArc(sketch, "E67.0", {"start": v(20.38, -7.18) * mm, "mid": v(11.96, -7.74) * mm, "end": v(4.2, -4.4) * mm});
            skArc(sketch, "E68.0", {"start": v(28.3, -9.98) * mm, "mid": v(24.8, -7.26) * mm, "end": v(20.38, -7.18) * mm});
            skArc(sketch, "E69.0", {"start": v(30.26, -12.43) * mm, "mid": v(29.23, -11.25) * mm, "end": v(28.3, -9.98) * mm});
            skArc(sketch, "E70.0", {"start": v(31.96, -19.07) * mm, "mid": v(31.98, -15.53) * mm, "end": v(30.26, -12.43) * mm});
            skLineSegment(sketch, "E71.0", {"start": v(29.84, -26.99) * mm, "end": v(31.96, -19.07) * mm});
            skArc(sketch, "E72.0", {"start": v(24.18, -32.1) * mm, "mid": v(27.76, -30.38) * mm, "end": v(29.84, -26.99) * mm});
            skArc(sketch, "E73.0", {"start": v(-24.18, -32.1) * mm, "mid": v(0, -34) * mm, "end": v(24.18, -32.1) * mm});
            skArc(sketch, "E74.0", {"start": v(-29.84, -26.99) * mm, "mid": v(-27.76, -30.38) * mm, "end": v(-24.18, -32.1) * mm});
            skSolve(sketch);
        }
        {
            var Q0;
            Q0=qCreatedBy(makeId("Right.planeOp"),FACE);
            var sketch = newSketch(context, id + "F29", { "sketchPlane" : qUnion([Q0])});
            skPoint(sketch, "E75", {"position": v(-4.23, -3) * mm});
            skLineSegment(sketch, "E76", {"start": v(-3.24, -3) * mm, "end": v(-12, -3) * mm, "construction": true});
            skLineSegment(sketch, "E77", {"start": v(-9, -3) * mm, "end": v(-10, -2) * mm});
            skLineSegment(sketch, "E78", {"start": v(-10, -2) * mm, "end": v(-10, -4) * mm});
            skLineSegment(sketch, "E79", {"start": v(-10, -4) * mm, "end": v(-9, -3) * mm});
            skSolve(sketch);
        }
        {
            var Q0;
            Q0 = qSketchRegion(id + "F29", true);
            var Q1;
            Q1 = qConstructionFilter(qBodyType(qCreatedBy(id + "F28" ,EDGE), BodyType.WIRE), ConstructionObject.NO);
            sweep(context, id + "F30", {"operationType" : NewBodyOperationType.REMOVE, "profiles" : qUnion([Q0]), "path" : qUnion([Q1])});
        }
    });
